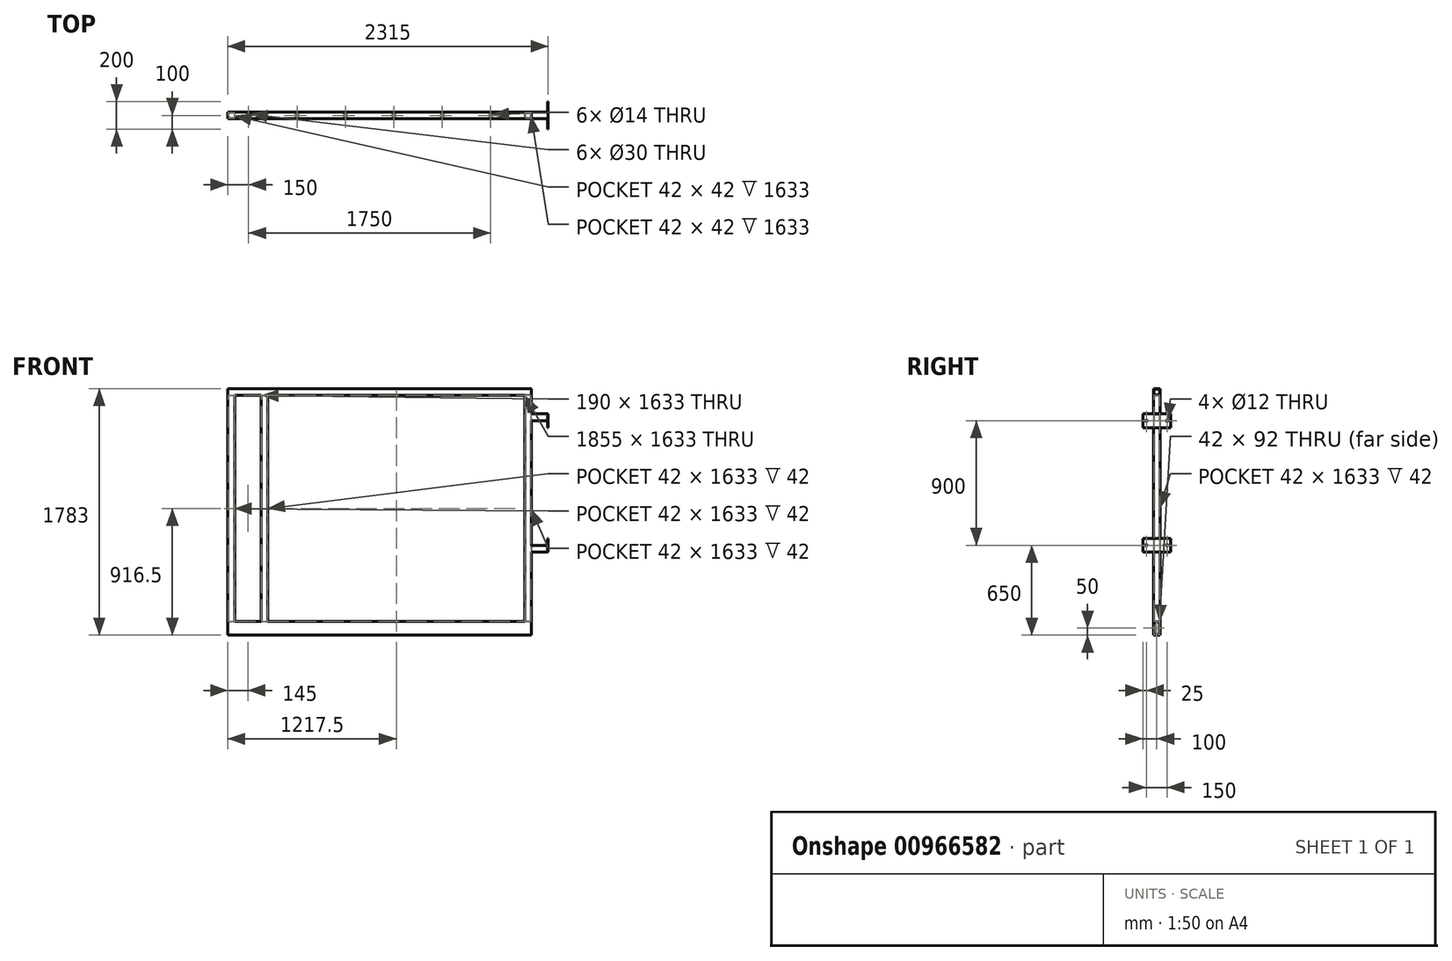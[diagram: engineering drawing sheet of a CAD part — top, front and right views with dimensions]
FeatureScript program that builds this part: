
annotation { "Feature Type Name" : "Feature", "Feature Type Description" : "" }
export const myFeature = defineFeature(function(context is Context, id is Id, definition is map)
    precondition{}
    {
        {
            var Q0;
            Q0=qCreatedBy(makeId("Top.planeOp"),FACE);
            var sketch = newSketch(context, id + "F0", { "sketchPlane" : qUnion([Q0])});
            skLineSegment(sketch, "E0.bottom", {"start": v(0, 0) * mm, "end": v(50, 0) * mm});
            skLineSegment(sketch, "E0.top", {"start": v(0, 50) * mm, "end": v(50, 50) * mm});
            skLineSegment(sketch, "E0.left", {"start": v(0, 0) * mm, "end": v(0, 4) * mm});
            skLineSegment(sketch, "E0.right", {"start": v(50, 0) * mm, "end": v(50, 50) * mm});
            skLineSegment(sketch, "E1.bottom", {"start": v(4, 46) * mm, "end": v(46, 46) * mm});
            skLineSegment(sketch, "E1.top", {"start": v(4, 4) * mm, "end": v(46, 4) * mm});
            skLineSegment(sketch, "E1.right", {"start": v(46, 46) * mm, "end": v(46, 4) * mm});
            skLineSegment(sketch, "E2", {"start": v(12.25, 50) * mm, "end": v(12.25, 46) * mm, "construction": true});
            skPoint(sketch, "E2.endSnap0", {"position": v(23, 46) * mm});
            skLineSegment(sketch, "E3", {"start": v(46, 38.8) * mm, "end": v(50, 38.8) * mm, "construction": true});
            skLineSegment(sketch, "E4", {"start": v(20.28, 4) * mm, "end": v(20.28, 0) * mm, "construction": true});
            skLineSegment(sketch, "E5.trimOffspring", {"start": v(0, 46) * mm, "end": v(0, 50) * mm});
            skLineSegment(sketch, "E6", {"start": v(0, 46) * mm, "end": v(0, 4) * mm});
            skLineSegment(sketch, "E7", {"start": v(4, 46) * mm, "end": v(4, 4) * mm});
            skSolve(sketch);
        }
        {
            var Q0;
            Q0=qSketchRegion(id+"F0",true);
            extrude(context, id + "F1", {"entities" : qUnion([Q0]), "depth" : (1783 - 150) * mm, "offsetDistance" : 25 * mm});
        }
        {
            var Q0;
            Q0=makeQuery(id+"F1.opExtrude","SWEPT_FACE",FACE,{"disambiguationData":[OSD([sQuery(id+"F0.wireOp",EDGE,"E5.trimOffspring")])]});
            var sketch = newSketch(context, id + "F2", { "sketchPlane" : qUnion([Q0])});
            skLineSegment(sketch, "E8.bottom", {"start": v(-50, 0) * mm, "end": v(0, 0) * mm});
            skLineSegment(sketch, "E8.top", {"start": v(-50, -100) * mm, "end": v(0, -100) * mm});
            skLineSegment(sketch, "E8.left", {"start": v(-50, 0) * mm, "end": v(-50, -100) * mm});
            skLineSegment(sketch, "E8.right", {"start": v(0, 0) * mm, "end": v(0, -100) * mm});
            skLineSegment(sketch, "E9.bottom", {"start": v(-46, -4) * mm, "end": v(-4, -4) * mm});
            skLineSegment(sketch, "E9.top", {"start": v(-46, -96) * mm, "end": v(-4, -96) * mm});
            skLineSegment(sketch, "E9.left", {"start": v(-50, -4) * mm, "end": v(-50, -96) * mm});
            skLineSegment(sketch, "E9.right", {"start": v(-4, -4) * mm, "end": v(-4, -96) * mm});
            skLineSegment(sketch, "E10", {"start": v(-25, 0) * mm, "end": v(-25, -4) * mm, "construction": true});
            skLineSegment(sketch, "E11", {"start": v(-50, -50) * mm, "end": v(-50, -50) * mm});
            skLineSegment(sketch, "E12", {"start": v(-25, -100) * mm, "end": v(-25, -96) * mm, "construction": true});
            skLineSegment(sketch, "E13", {"start": v(-4, -50) * mm, "end": v(0, -50) * mm, "construction": true});
            skLineSegment(sketch, "E14", {"start": v(-46, -4) * mm, "end": v(-46, -96) * mm});
            skLineSegment(sketch, "E15", {"start": v(-46, -50) * mm, "end": v(-50, -50) * mm, "construction": true});
            skSolve(sketch);
        }
        {
            var Q0;
            Q0=makeQuery(id+"F2.imprint","IMPRINT",FACE,{"disambiguationData":[TD([[makeQuery(id+"F2.imprint","IMPRINT",EDGE,{"derivedFrom":sQuery(id+"F2.wireOp",EDGE,"E8.top")}),1.0]])]});
            extrude(context, id + "F3", {"entities" : qUnion([Q0]), "oppositeDirection" : true, "depth" : 2195 * mm, "offsetDistance" : 25 * mm});
        }
        {
            var Q0;
            Q0=qCreatedBy(makeId("Right.planeOp"),FACE);
            cPlane(context, id + "F4", {"entities" : qUnion([Q0]), "cplaneType" : CPlaneType.OFFSET, "offset" : (2195 / 2) * mm, "width" : 150 * mm, "height" : 150 * mm});
        }
        {
            var Q0;
            Q0=makeQuery(id+"F1.opExtrude","SWEPT_BODY",BODY,{"disambiguationData":[OSD([sQuery(id+"F0.wireOp",EDGE,"E0.bottom"),sQuery(id+"F0.wireOp",EDGE,"E0.top"),sQuery(id+"F0.wireOp",EDGE,"E0.left"),sQuery(id+"F0.wireOp",EDGE,"E0.right"),sQuery(id+"F0.wireOp",EDGE,"E1.bottom"),sQuery(id+"F0.wireOp",EDGE,"E1.top"),sQuery(id+"F0.wireOp",EDGE,"E1.right"),sQuery(id+"F0.wireOp",EDGE,"E5.trimOffspring")])]});
            var Q1;
            Q1=qCreatedBy(id+"F4.planeOp",FACE);
            mirror(context, id + "F5", {"operationType" : NewBodyOperationType.ADD, "entities" : qUnion([Q0]), "mirrorPlane" : qUnion([Q1])});
        }
        {
            var Q0;
            Q0=makeQuery(id+"F5.boolean.opBoolean","MERGE",FACE,{"derivedFrom":[makeQuery(id+"F1.opExtrude","SWEPT_FACE",FACE,{"disambiguationData":[OSD([sQuery(id+"F0.wireOp",EDGE,"E0.left")])]}),makeQuery(id+"F1.opExtrude","SWEPT_FACE",FACE,{"disambiguationData":[OSD([sQuery(id+"F0.wireOp",EDGE,"E5.trimOffspring")])]}),makeQuery(id+"F3.opExtrude","CAP_FACE",FACE,{"disambiguationData":[OSD([sQuery(id+"F2.wireOp",EDGE,"E8.bottom"),sQuery(id+"F2.wireOp",EDGE,"E8.top"),sQuery(id+"F2.wireOp",EDGE,"E8.left"),sQuery(id+"F2.wireOp",EDGE,"E8.right"),sQuery(id+"F2.wireOp",EDGE,"E9.bottom"),sQuery(id+"F2.wireOp",EDGE,"E9.top"),sQuery(id+"F2.wireOp",EDGE,"E9.left"),sQuery(id+"F2.wireOp",EDGE,"E9.right")])],"isStart":true})]});
            var sketch = newSketch(context, id + "F6", { "sketchPlane" : qUnion([Q0])});
            skLineSegment(sketch, "E16.bottom", {"start": v(-50, 1683) * mm, "end": v(-46, 1683) * mm});
            skLineSegment(sketch, "E16.top", {"start": v(-50, 1633) * mm, "end": v(0, 1633) * mm});
            skLineSegment(sketch, "E16.left", {"start": v(-50, 1683) * mm, "end": v(-50, 1633) * mm});
            skLineSegment(sketch, "E16.right", {"start": v(0, 1683) * mm, "end": v(0, 1633) * mm});
            skLineSegment(sketch, "E17.top", {"start": v(-46, 1637) * mm, "end": v(-4, 1637) * mm});
            skLineSegment(sketch, "E17.left", {"start": v(-46, 1679) * mm, "end": v(-46, 1637) * mm});
            skLineSegment(sketch, "E17.right", {"start": v(-4, 1679) * mm, "end": v(-4, 1637) * mm});
            skLineSegment(sketch, "E18", {"start": v(-25, 1637) * mm, "end": v(-25, 1633) * mm, "construction": true});
            skLineSegment(sketch, "E19.trimOffspring", {"start": v(-4, 1683) * mm, "end": v(0, 1683) * mm});
            skLineSegment(sketch, "E20", {"start": v(-4, 1679) * mm, "end": v(-46, 1679) * mm});
            skLineSegment(sketch, "E21", {"start": v(-46, 1683) * mm, "end": v(-4, 1683) * mm});
            skSolve(sketch);
        }
        {
            var Q0;
            Q0=qSketchRegion(id+"F6",true);
            var Q1;
            Q1=makeQuery(id+"F5.boolean.opBoolean","MERGE",FACE,{"derivedFrom":[makeQuery(id+"F3.opExtrude","CAP_FACE",FACE,{"disambiguationData":[OSD([sQuery(id+"F2.wireOp",EDGE,"E8.bottom"),sQuery(id+"F2.wireOp",EDGE,"E8.top"),sQuery(id+"F2.wireOp",EDGE,"E8.left"),sQuery(id+"F2.wireOp",EDGE,"E8.right"),sQuery(id+"F2.wireOp",EDGE,"E9.bottom"),sQuery(id+"F2.wireOp",EDGE,"E9.top"),sQuery(id+"F2.wireOp",EDGE,"E9.left"),sQuery(id+"F2.wireOp",EDGE,"E9.right")])],"isStart":false}),makeQuery(id+"F5.opPattern","COPY",FACE,{"derivedFrom":makeQuery(id+"F1.opExtrude","SWEPT_FACE",FACE,{"disambiguationData":[OSD([sQuery(id+"F0.wireOp",EDGE,"E0.left")])]}),"instanceName":"1"}),makeQuery(id+"F5.opPattern","COPY",FACE,{"derivedFrom":makeQuery(id+"F1.opExtrude","SWEPT_FACE",FACE,{"disambiguationData":[OSD([sQuery(id+"F0.wireOp",EDGE,"E5.trimOffspring")])]}),"instanceName":"1"})]});
            extrude(context, id + "F7", {"entities" : qUnion([Q0]), "operationType" : NewBodyOperationType.ADD, "endBound" : BoundingType.UP_TO_SURFACE, "oppositeDirection" : true, "depth" : 25 * mm, "endBoundEntityFace" : qUnion([Q1]), "offsetDistance" : 25 * mm});
        }
        {
            var Q0;
            Q0=makeQuery(id+"F7.boolean.opBoolean","MERGE",FACE,{"derivedFrom":[makeQuery(id+"F5.boolean.opBoolean","MERGE",FACE,{"derivedFrom":[makeQuery(id+"F3.opExtrude","CAP_FACE",FACE,{"disambiguationData":[OSD([sQuery(id+"F2.wireOp",EDGE,"E8.bottom"),sQuery(id+"F2.wireOp",EDGE,"E8.top"),sQuery(id+"F2.wireOp",EDGE,"E8.left"),sQuery(id+"F2.wireOp",EDGE,"E8.right"),sQuery(id+"F2.wireOp",EDGE,"E9.bottom"),sQuery(id+"F2.wireOp",EDGE,"E9.top"),sQuery(id+"F2.wireOp",EDGE,"E9.left"),sQuery(id+"F2.wireOp",EDGE,"E9.right")])],"isStart":false}),makeQuery(id+"F5.opPattern","COPY",FACE,{"derivedFrom":makeQuery(id+"F1.opExtrude","SWEPT_FACE",FACE,{"disambiguationData":[OSD([sQuery(id+"F0.wireOp",EDGE,"E0.left")])]}),"instanceName":"1"}),makeQuery(id+"F5.opPattern","COPY",FACE,{"derivedFrom":makeQuery(id+"F1.opExtrude","SWEPT_FACE",FACE,{"disambiguationData":[OSD([sQuery(id+"F0.wireOp",EDGE,"E5.trimOffspring")])]}),"instanceName":"1"})]}),makeQuery(id+"F7.opExtrude","CAP_FACE",FACE,{"disambiguationData":[OSD([sQuery(id+"F6.wireOp",EDGE,"E16.bottom"),sQuery(id+"F6.wireOp",EDGE,"E16.top"),sQuery(id+"F6.wireOp",EDGE,"E16.left"),sQuery(id+"F6.wireOp",EDGE,"E16.right"),sQuery(id+"F6.wireOp",EDGE,"E17.top"),sQuery(id+"F6.wireOp",EDGE,"E17.left"),sQuery(id+"F6.wireOp",EDGE,"E17.right"),sQuery(id+"F6.wireOp",EDGE,"E19.trimOffspring")])],"isStart":false})]});
            var sketch = newSketch(context, id + "F8", { "sketchPlane" : qUnion([Q0])});
            skLineSegment(sketch, "E22.bottom", {"start": v(0, 550) * mm, "end": v(4, 550) * mm});
            skLineSegment(sketch, "E22.top", {"start": v(0, 500) * mm, "end": v(50, 500) * mm});
            skLineSegment(sketch, "E22.left", {"start": v(0, 550) * mm, "end": v(0, 500) * mm});
            skLineSegment(sketch, "E22.right", {"start": v(50, 550) * mm, "end": v(50, 500) * mm});
            skLineSegment(sketch, "E23.top", {"start": v(4, 504) * mm, "end": v(46, 504) * mm});
            skLineSegment(sketch, "E23.left", {"start": v(4, 550) * mm, "end": v(4, 504) * mm});
            skLineSegment(sketch, "E23.right", {"start": v(46, 550) * mm, "end": v(46, 504) * mm});
            skLineSegment(sketch, "E24.trimOffspring", {"start": v(46, 550) * mm, "end": v(50, 550) * mm});
            skLineSegment(sketch, "E25", {"start": v(-400.98, 1000) * mm, "end": v(496.26, 1000) * mm, "construction": true});
            skLineSegment(sketch, "E26.MirrorCS", {"start": v(0, 1450) * mm, "end": v(4, 1450) * mm});
            skLineSegment(sketch, "E27.MirrorCS", {"start": v(46, 1450) * mm, "end": v(50, 1450) * mm});
            skLineSegment(sketch, "E28.MirrorCS", {"start": v(46, 1450) * mm, "end": v(46, 1496) * mm});
            skLineSegment(sketch, "E29.MirrorCS", {"start": v(50, 1450) * mm, "end": v(50, 1500) * mm});
            skLineSegment(sketch, "E30.MirrorCS", {"start": v(0, 1450) * mm, "end": v(0, 1500) * mm});
            skLineSegment(sketch, "E31.MirrorCS", {"start": v(4, 1496) * mm, "end": v(46, 1496) * mm});
            skLineSegment(sketch, "E32.MirrorCS", {"start": v(4, 1450) * mm, "end": v(4, 1496) * mm});
            skLineSegment(sketch, "E33.MirrorCS", {"start": v(0, 1500) * mm, "end": v(50, 1500) * mm});
            skSolve(sketch);
        }
        {
            var Q0;
            Q0=qSketchRegion(id+"F8",true);
            extrude(context, id + "F9", {"entities" : qUnion([Q0]), "operationType" : NewBodyOperationType.ADD, "depth" : 116 * mm, "offsetDistance" : 25 * mm});
        }
        {
            var Q0;
            Q0=makeQuery(id+"F9.opExtrude","CAP_FACE",FACE,{"disambiguationData":[OSD([sQuery(id+"F8.wireOp",EDGE,"E26.MirrorCS"),sQuery(id+"F8.wireOp",EDGE,"E27.MirrorCS"),sQuery(id+"F8.wireOp",EDGE,"E28.MirrorCS"),sQuery(id+"F8.wireOp",EDGE,"E29.MirrorCS"),sQuery(id+"F8.wireOp",EDGE,"E30.MirrorCS"),sQuery(id+"F8.wireOp",EDGE,"E31.MirrorCS"),sQuery(id+"F8.wireOp",EDGE,"E32.MirrorCS"),sQuery(id+"F8.wireOp",EDGE,"E33.MirrorCS")])],"isStart":false});
            var sketch = newSketch(context, id + "F10", { "sketchPlane" : qUnion([Q0])});
            skLineSegment(sketch, "E34.bottom", {"start": v(125, 1500) * mm, "end": v(-75, 1500) * mm});
            skLineSegment(sketch, "E34.top", {"start": v(125, 1400) * mm, "end": v(-75, 1400) * mm});
            skLineSegment(sketch, "E34.left", {"start": v(125, 1500) * mm, "end": v(125, 1400) * mm});
            skLineSegment(sketch, "E34.right", {"start": v(-75, 1500) * mm, "end": v(-75, 1400) * mm});
            skPoint(sketch, "E35", {"position": v(25, 1500) * mm});
            skLineSegment(sketch, "E36.bottom", {"start": v(125, 600) * mm, "end": v(-75, 600) * mm});
            skLineSegment(sketch, "E36.top", {"start": v(125, 500) * mm, "end": v(-75, 500) * mm});
            skLineSegment(sketch, "E36.left", {"start": v(125, 600) * mm, "end": v(125, 500) * mm});
            skLineSegment(sketch, "E36.right", {"start": v(-75, 600) * mm, "end": v(-75, 500) * mm});
            skPoint(sketch, "E37", {"position": v(25, 500) * mm});
            skCircle(sketch, "E38", {"center": v(100, 1450) * mm, "radius": 6 * mm});
            skLineSegment(sketch, "E39", {"start": v(-50, 1450) * mm, "end": v(100, 1450) * mm, "construction": true});
            skLineSegment(sketch, "E40", {"start": v(25, 1400) * mm, "end": v(25, 1450) * mm, "construction": true});
            skLineSegment(sketch, "E41", {"start": v(-50, 550) * mm, "end": v(100, 550) * mm, "construction": true});
            skPoint(sketch, "E41.startSnap0", {"position": v(-75, 550) * mm});
            skLineSegment(sketch, "E42", {"start": v(25, 550) * mm, "end": v(25, 500) * mm, "construction": true});
            skCircle(sketch, "E43", {"center": v(-50, 550) * mm, "radius": 6 * mm});
            skCircle(sketch, "E44", {"center": v(100, 550) * mm, "radius": 6 * mm});
            skCircle(sketch, "E45", {"center": v(-50, 1450) * mm, "radius": 6 * mm});
            skSolve(sketch);
        }
        {
            var Q0;
            Q0=qSketchRegion(id+"F10",true);
            extrude(context, id + "F11", {"entities" : qUnion([Q0]), "operationType" : NewBodyOperationType.ADD, "depth" : 4 * mm, "offsetDistance" : 25 * mm});
        }
        {
            var Q0;
            {var subQ2=makeQuery(id+"F1.opExtrude","SWEPT_FACE",FACE,{"disambiguationData":[OSD([sQuery(id+"F0.wireOp",EDGE,"E0.bottom")])]});Q0=makeQuery(id+"F5.boolean.opBoolean","SPLIT",FACE,{"disambiguationData":[TD([subQ2])],"derivedFrom":makeQuery(id+"F3.opExtrude","SWEPT_FACE",FACE,{"disambiguationData":[OSD([sQuery(id+"F2.wireOp",EDGE,"E8.bottom")])]})});}
            var sketch = newSketch(context, id + "F12", { "sketchPlane" : qUnion([Q0])});
            skLineSegment(sketch, "E46.bottom", {"start": v(290, 0) * mm, "end": v(240, 0) * mm});
            skLineSegment(sketch, "E46.top", {"start": v(290, 50) * mm, "end": v(240, 50) * mm});
            skLineSegment(sketch, "E46.left", {"start": v(290, 0) * mm, "end": v(290, 50) * mm});
            skLineSegment(sketch, "E46.right", {"start": v(240, 0) * mm, "end": v(240, 50) * mm});
            skLineSegment(sketch, "E47.bottom", {"start": v(244, 46) * mm, "end": v(286, 46) * mm});
            skLineSegment(sketch, "E47.top", {"start": v(244, 4) * mm, "end": v(286, 4) * mm});
            skLineSegment(sketch, "E47.left", {"start": v(244, 46) * mm, "end": v(244, 4) * mm});
            skLineSegment(sketch, "E47.right", {"start": v(286, 46) * mm, "end": v(286, 4) * mm});
            skSolve(sketch);
        }
        {
            var Q0;
            Q0=qSketchRegion(id+"F12",true);
            var Q1;
            {var subQ2=makeQuery(id+"F1.opExtrude","SWEPT_FACE",FACE,{"disambiguationData":[OSD([sQuery(id+"F0.wireOp",EDGE,"E0.bottom")])]});Q1=makeQuery(id+"F7.boolean.opBoolean","SPLIT",FACE,{"disambiguationData":[TD([subQ2])],"derivedFrom":makeQuery(id+"F7.opExtrude","SWEPT_FACE",FACE,{"disambiguationData":[OSD([sQuery(id+"F6.wireOp",EDGE,"E16.top")])]})});}
            extrude(context, id + "F13", {"entities" : qUnion([Q0]), "operationType" : NewBodyOperationType.ADD, "endBound" : BoundingType.UP_TO_SURFACE, "depth" : 25 * mm, "endBoundEntityFace" : qUnion([Q1]), "offsetDistance" : 25 * mm});
        }
        {
            var Q0;
            Q0=makeQuery(id+"F3.opExtrude","SWEPT_FACE",FACE,{"disambiguationData":[OSD([sQuery(id+"F2.wireOp",EDGE,"E8.top")])]});
            var sketch = newSketch(context, id + "F14", { "sketchPlane" : qUnion([Q0])});
            skLineSegment(sketch, "E48", {"start": v(0, -25) * mm, "end": v(2195, -25) * mm, "construction": true});
            skCircle(sketch, "E49", {"center": v(150, -25) * mm, "radius": 7 * mm});
            skCircle(sketch, "E50.1.0.0", {"center": v(500, -25) * mm, "radius": 7 * mm});
            skCircle(sketch, "E50.2.0.0", {"center": v(850, -25) * mm, "radius": 7 * mm});
            skCircle(sketch, "E50.3.0.0", {"center": v(1200, -25) * mm, "radius": 7 * mm});
            skCircle(sketch, "E50.4.0.0", {"center": v(1550, -25) * mm, "radius": 7 * mm});
            skCircle(sketch, "E50.5.0.0", {"center": v(1900, -25) * mm, "radius": 7 * mm});
            skCircle(sketch, "E50.6.0.0", {"center": v(2250, -25) * mm, "radius": 7 * mm});
            skLineSegment(sketch, "E50.direction1", {"start": v(150, -25) * mm, "end": v(500, -25) * mm, "construction": true});
            skSolve(sketch);
        }
        {
            var Q0;
            Q0=qSketchRegion(id+"F14",true);
            var Q1;
            Q1=qConstructionFilter(qBodyType(qCreatedBy(id+"F14",EDGE),BodyType.WIRE),ConstructionObject.NO);
            extrude(context, id + "F15", {"entities" : qUnion([Q0]), "operationType" : NewBodyOperationType.REMOVE, "surfaceEntities" : qUnion([Q1]), "oppositeDirection" : true, "depth" : 125 * mm, "offsetDistance" : 25 * mm});
        }
        {
            var Q0;
            {var subQ2=makeQuery(id+"F1.opExtrude","SWEPT_FACE",FACE,{"disambiguationData":[OSD([sQuery(id+"F0.wireOp",EDGE,"E0.right")])]});var subQ3=makeQuery(id+"F5.opPattern","COPY",FACE,{"derivedFrom":subQ2,"instanceName":"1"});var subQ4=makeQuery(id+"F1.opExtrude","SWEPT_FACE",FACE,{"disambiguationData":[OSD([sQuery(id+"F0.wireOp",EDGE,"E0.bottom")])]});Q0=makeQuery(id+"F13.boolean.opBoolean","SPLIT",FACE,{"disambiguationData":[TD([subQ3])],"derivedFrom":makeQuery(id+"F5.boolean.opBoolean","SPLIT",FACE,{"disambiguationData":[TD([subQ4])],"derivedFrom":makeQuery(id+"F3.opExtrude","SWEPT_FACE",FACE,{"disambiguationData":[OSD([sQuery(id+"F2.wireOp",EDGE,"E8.bottom")])]})})});}
            var sketch = newSketch(context, id + "F16", { "sketchPlane" : qUnion([Q0])});
            skCircle(sketch, "E51", {"center": v(150, 25) * mm, "radius": 15 * mm});
            skCircle(sketch, "E52.1.0.0", {"center": v(500, 25) * mm, "radius": 15 * mm});
            skCircle(sketch, "E52.2.0.0", {"center": v(850, 25) * mm, "radius": 15 * mm});
            skCircle(sketch, "E52.3.0.0", {"center": v(1200, 25) * mm, "radius": 15 * mm});
            skCircle(sketch, "E52.4.0.0", {"center": v(1550, 25) * mm, "radius": 15 * mm});
            skCircle(sketch, "E52.5.0.0", {"center": v(1900, 25) * mm, "radius": 15 * mm});
            skLineSegment(sketch, "E52.direction1", {"start": v(150, 25) * mm, "end": v(500, 25) * mm, "construction": true});
            skSolve(sketch);
        }
        {
            var Q0;
            Q0=makeQuery(id+"F16.imprint","IMPRINT",FACE,{"disambiguationData":[TD([[makeQuery(id+"F16.imprint","IMPRINT",EDGE,{"derivedFrom":sQuery(id+"F16.wireOp",EDGE,"E52.1.0.0")}),1.0]])]});
            var Q1;
            Q1=makeQuery(id+"F16.imprint","IMPRINT",FACE,{"disambiguationData":[TD([[makeQuery(id+"F16.imprint","IMPRINT",EDGE,{"derivedFrom":sQuery(id+"F16.wireOp",EDGE,"E52.2.0.0")}),1.0]])]});
            var Q2;
            Q2=makeQuery(id+"F16.imprint","IMPRINT",FACE,{"disambiguationData":[TD([[makeQuery(id+"F16.imprint","IMPRINT",EDGE,{"derivedFrom":sQuery(id+"F16.wireOp",EDGE,"E52.3.0.0")}),1.0]])]});
            var Q3;
            Q3=makeQuery(id+"F16.imprint","IMPRINT",FACE,{"disambiguationData":[TD([[makeQuery(id+"F16.imprint","IMPRINT",EDGE,{"derivedFrom":sQuery(id+"F16.wireOp",EDGE,"E52.4.0.0")}),1.0]])]});
            var Q4;
            Q4=makeQuery(id+"F16.imprint","IMPRINT",FACE,{"disambiguationData":[TD([[makeQuery(id+"F16.imprint","IMPRINT",EDGE,{"derivedFrom":sQuery(id+"F16.wireOp",EDGE,"E52.5.0.0")}),1.0]])]});
            var Q5;
            Q5=makeQuery(id+"F16.imprint","IMPRINT",FACE,{"disambiguationData":[TD([[makeQuery(id+"F16.imprint","IMPRINT",EDGE,{"derivedFrom":sQuery(id+"F16.wireOp",EDGE,"E52.6.0.0")}),1.0]])]});
            var Q6;
            Q6=makeQuery(id+"F16.imprint","IMPRINT",FACE,{"disambiguationData":[TD([[makeQuery(id+"F16.imprint","IMPRINT",EDGE,{"derivedFrom":sQuery(id+"F16.wireOp",EDGE,"E51")}),1.0]])]});
            var Q7;
            Q7=qConstructionFilter(qBodyType(qCreatedBy(id+"F16",EDGE),BodyType.WIRE),ConstructionObject.NO);
            extrude(context, id + "F17", {"entities" : qUnion([Q0, Q1, Q2, Q3, Q4, Q5, Q6]), "operationType" : NewBodyOperationType.REMOVE, "surfaceEntities" : qUnion([Q7]), "oppositeDirection" : true, "depth" : 5 * mm, "offsetDistance" : 25 * mm});
        }
    });
